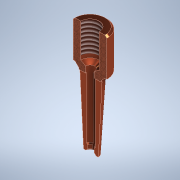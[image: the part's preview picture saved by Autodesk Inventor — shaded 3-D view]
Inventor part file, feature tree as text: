
AUTODESK INVENTOR PART (.ipt)
format: ipt  version: 2022 (Build 260153000, 153)  size: 194,560 bytes
history: native  units: mm
features: sketch x3, chamfer x2, revolve x1, hole x1, extrude x1
ambient origin geometry x8: Origin, YZ Plane, XZ Plane, XY Plane, X Axis, Y Axis, Z Axis, Center Point
bodies: Solid1 (feature_tree)
feature tree (8):
  revolve  "Revolution1"  [1 undecoded]
  hole  "Hole1"  [1 undecoded]
  chamfer  "Chamfer2"  Distance=5.0mm
  extrude  "Extrusion1"  Depth=0.25mm
  chamfer  "Chamfer3"  Distance=8.0mm
  sketch  "Sketch1"  dims[d0=4.5mm d1=0.9mm]
  sketch  "Sketch2"  dims[d2=1.2mm d3=135.0deg]
  sketch  "Sketch3"  dims[d4=3.0mm d5=5.0mm d6=0.8mm d7=8.0mm d8=0.25mm d9=0.5mm d10=0.5mm d11=0.3mm d12=360.0deg d13=0.25mm d14=0.25mm d15=9.0mm d16=0.0mm d20=2.459mm d21=4.0mm d22=6.3mm d23=2.0mm d24=90.0deg d25=4.5mm d26=20.594885mm d27=0.25mm d28=2.0mm d29=45.0deg d30=0.5mm d31=2.0mm d32=45.0deg]
note: 2 required parameter values undecoded (feature->parameter linkage not recoverable at this tier; creation-order binding heuristic only, values carry confidence <= 0.55)